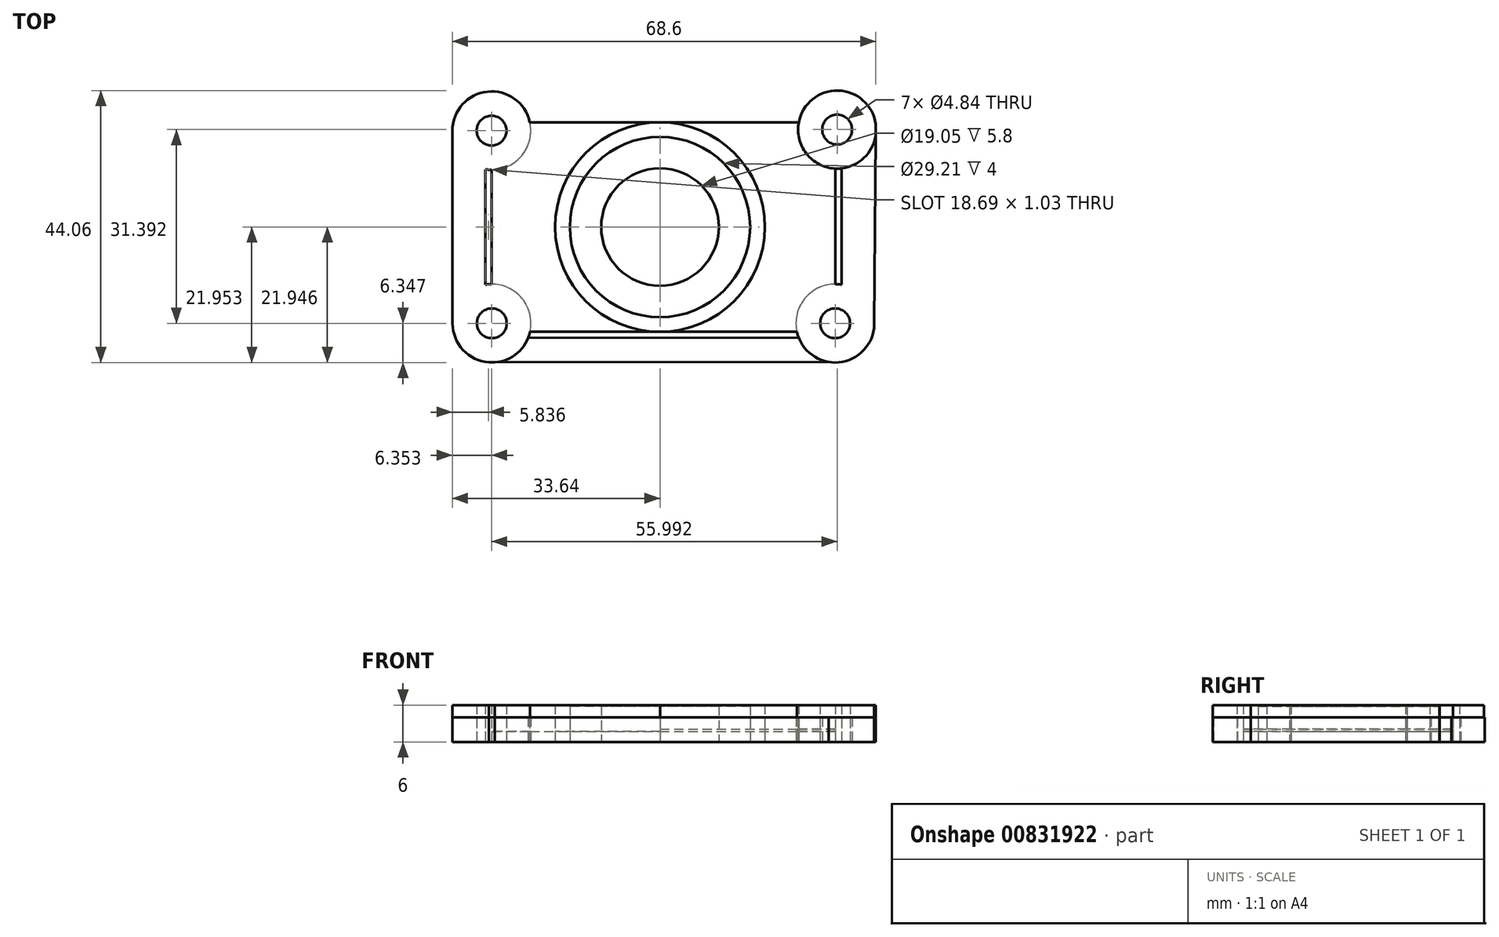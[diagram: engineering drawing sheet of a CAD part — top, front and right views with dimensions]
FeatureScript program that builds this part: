
annotation { "Feature Type Name" : "Feature", "Feature Type Description" : "" }
export const myFeature = defineFeature(function(context is Context, id is Id, definition is map)
    precondition{}
    {
        {
            var Q0;
            Q0=qCreatedBy(makeId("Top.planeOp"),FACE);
            var sketch = newSketch(context, id + "F0", { "sketchPlane" : qUnion([Q0])});
            skCircle(sketch, "E0", {"center": v(14.81, -5.47) * mm, "radius": 6.35 * mm});
            skLineSegment(sketch, "E1", {"start": v(14.81, 0.88) * mm, "end": v(69.45, 0.88) * mm});
            skCircle(sketch, "E2", {"center": v(70.8, -5.3) * mm, "radius": 6.32 * mm});
            skCircle(sketch, "E3", {"center": v(14.85, -36.7) * mm, "radius": 6.35 * mm});
            skLineSegment(sketch, "E4", {"start": v(8.46, -5.47) * mm, "end": v(8.5, -36.7) * mm});
            skCircle(sketch, "E5", {"center": v(70.48, -36.7) * mm, "radius": 6.35 * mm});
            skLineSegment(sketch, "E6", {"start": v(76.83, -36.9) * mm, "end": v(77.06, -4.38) * mm});
            skLineSegment(sketch, "E7.trimOffspring", {"start": v(14.4, -43.03) * mm, "end": v(69.46, -42.96) * mm});
            skCircle(sketch, "E8", {"center": v(42.1, -21.1) * mm, "radius": 16.98 * mm});
            skCircle(sketch, "E9", {"center": v(42.1, -21.1) * mm, "radius": 14.6 * mm});
            skCircle(sketch, "E10", {"center": v(42.1, -21.1) * mm, "radius": 9.53 * mm});
            skLineSegment(sketch, "E11", {"start": v(70.48, -11.62) * mm, "end": v(70.48, -30.34) * mm});
            skLineSegment(sketch, "E12", {"start": v(21.01, -4.1) * mm, "end": v(64.6, -4.1) * mm});
            skLineSegment(sketch, "E13", {"start": v(14.81, -30.34) * mm, "end": v(14.81, -11.82) * mm});
            skLineSegment(sketch, "E14", {"start": v(21.05, -38.08) * mm, "end": v(64.28, -38.08) * mm});
            skLineSegment(sketch, "E15", {"start": v(20.73, -39.09) * mm, "end": v(64.58, -39.03) * mm});
            skLineSegment(sketch, "E16", {"start": v(71.51, -30.43) * mm, "end": v(71.51, -11.58) * mm});
            skLineSegment(sketch, "E17", {"start": v(13.78, -30.43) * mm, "end": v(13.78, -11.74) * mm});
            skLineSegment(sketch, "E18", {"start": v(20.68, -3.04) * mm, "end": v(64.9, -3.04) * mm});
            skCircle(sketch, "E19", {"center": v(14.81, -5.47) * mm, "radius": 2.42 * mm});
            skCircle(sketch, "E20", {"center": v(14.85, -36.7) * mm, "radius": 2.42 * mm});
            skCircle(sketch, "E21", {"center": v(70.48, -36.7) * mm, "radius": 2.42 * mm});
            skCircle(sketch, "E22", {"center": v(70.8, -5.3) * mm, "radius": 2.42 * mm});
            skPoint(sketch, "E23.visualSharp", {"position": v(71.51, -10.41) * mm});
            skPoint(sketch, "E24.orphan", {"position": v(13.78, -10.53) * mm});
            skPoint(sketch, "E25.orphan", {"position": v(14.81, -10.63) * mm});
            skPoint(sketch, "E26.orphan", {"position": v(13.78, -31.65) * mm});
            skPoint(sketch, "E27.orphan", {"position": v(14.81, -31.53) * mm});
            skPoint(sketch, "E28.orphan", {"position": v(70.48, -31.53) * mm});
            skPoint(sketch, "E29.end.orphan", {"position": v(70.48, -10.45) * mm});
            skSolve(sketch);
        }
        {
            var Q0;
            {var subQ0=sQuery(id+"F0.wireOp",EDGE,"E16");var subQ1=sQuery(id+"F0.wireOp",EDGE,"E2");var subQ2=makeQuery(id+"F0.imprint","INTERSECT",VERTEX,{"derivedFrom":[subQ1,subQ0]});Q0=makeQuery(id+"F0.imprint","IMPRINT",FACE,{"disambiguationData":[TD([[makeQuery(id+"F0.imprint","IMPRINT",EDGE,{"disambiguationData":[TD([[subQ2,-1.0]])],"derivedFrom":subQ1}),-1.0]])]});}
            var Q1;
            Q1=makeQuery(id+"F0.imprint","IMPRINT",FACE,{"disambiguationData":[TD([[makeQuery(id+"F0.imprint","IMPRINT",EDGE,{"derivedFrom":sQuery(id+"F0.wireOp",EDGE,"E21")}),-1.0]])]});
            var Q2;
            {var subQ0=sQuery(id+"F0.wireOp",EDGE,"E7.trimOffspring");var subQ1=sQuery(id+"F0.wireOp",EDGE,"E3");var subQ2=makeQuery(id+"F0.imprint","INTERSECT",VERTEX,{"disambiguationData":[OD(1.0)],"derivedFrom":[subQ1,subQ0]});Q2=makeQuery(id+"F0.imprint","IMPRINT",FACE,{"disambiguationData":[TD([[makeQuery(id+"F0.imprint","IMPRINT",EDGE,{"disambiguationData":[TD([[subQ2,-1.0]])],"derivedFrom":subQ1}),-1.0]])]});}
            var Q3;
            Q3=makeQuery(id+"F0.imprint","IMPRINT",FACE,{"disambiguationData":[TD([[makeQuery(id+"F0.imprint","IMPRINT",EDGE,{"derivedFrom":sQuery(id+"F0.wireOp",EDGE,"E20")}),-1.0]])]});
            var Q4;
            {var subQ0=sQuery(id+"F0.wireOp",EDGE,"E4");Q4=makeQuery(id+"F0.imprint","IMPRINT",FACE,{"disambiguationData":[TD([[makeQuery(id+"F0.imprint","IMPRINT",EDGE,{"derivedFrom":subQ0}),1.0]])]});}
            var Q5;
            Q5=makeQuery(id+"F0.imprint","IMPRINT",FACE,{"disambiguationData":[TD([[makeQuery(id+"F0.imprint","IMPRINT",EDGE,{"derivedFrom":sQuery(id+"F0.wireOp",EDGE,"E19")}),-1.0]])]});
            var Q6;
            {var subQ0=sQuery(id+"F0.wireOp",EDGE,"E1");Q6=makeQuery(id+"F0.imprint","IMPRINT",FACE,{"disambiguationData":[TD([[makeQuery(id+"F0.imprint","IMPRINT",EDGE,{"derivedFrom":subQ0}),-1.0]])]});}
            var Q7;
            {var subQ10=sQuery(id+"F0.wireOp",EDGE,"ZcBLGhaq-u4ml-COmK-nmpy-0ZbfGJL8DPDr");Q7=makeQuery(id+"F0.imprint","IMPRINT",FACE,{"disambiguationData":[TD([[makeQuery(id+"F0.imprint","IMPRINT",EDGE,{"derivedFrom":subQ10}),1.0]])]});}
            var Q8;
            {var subQ0=sQuery(id+"F0.wireOp",EDGE,"E12");var subQ1=sQuery(id+"F0.wireOp",EDGE,"E0");var subQ2=makeQuery(id+"F0.imprint","INTERSECT",VERTEX,{"derivedFrom":[subQ1,subQ0]});Q8=makeQuery(id+"F0.imprint","IMPRINT",FACE,{"disambiguationData":[TD([[makeQuery(id+"F0.imprint","IMPRINT",EDGE,{"disambiguationData":[TD([[subQ2,1.0]])],"derivedFrom":subQ1}),-1.0]])]});}
            var Q9;
            {var subQ1=sQuery(id+"F0.wireOp",EDGE,"E2");var subQ9=sQuery(id+"F0.wireOp",EDGE,"E12");var subQ11=makeQuery(id+"F0.imprint","INTERSECT",VERTEX,{"derivedFrom":[subQ1,subQ9]});Q9=makeQuery(id+"F0.imprint","IMPRINT",FACE,{"disambiguationData":[TD([[makeQuery(id+"F0.imprint","IMPRINT",EDGE,{"disambiguationData":[TD([[subQ11,-1.0]])],"derivedFrom":subQ1}),-1.0]])]});}
            extrude(context, id + "F1", {"entities" : qUnion([Q0, Q1, Q2, Q3, Q4, Q5, Q6, Q7, Q8, Q9]), "depth" : 6 * mm, "offsetDistance" : 25 * mm});
        }
        {
            var Q0;
            Q0=makeQuery(id+"F0.imprint","IMPRINT",FACE,{"disambiguationData":[TD([[makeQuery(id+"F0.imprint","IMPRINT",EDGE,{"derivedFrom":sQuery(id+"F0.wireOp",EDGE,"E9")}),1.0]])]});
            extrude(context, id + "F2", {"entities" : qUnion([Q0]), "depth" : 5.8 * mm, "offsetDistance" : 25 * mm});
        }
        {
            var Q0;
            Q0=makeQuery(id+"F0.imprint","IMPRINT",FACE,{"disambiguationData":[TD([[makeQuery(id+"F0.imprint","IMPRINT",EDGE,{"derivedFrom":sQuery(id+"F0.wireOp",EDGE,"E9")}),-1.0]])]});
            extrude(context, id + "F3", {"entities" : qUnion([Q0]), "depth" : 4 * mm, "offsetDistance" : 25 * mm});
        }
        {
            var Q0;
            Q0=makeQuery(id+"F0.imprint","IMPRINT",FACE,{"disambiguationData":[TD([[makeQuery(id+"F0.imprint","IMPRINT",EDGE,{"derivedFrom":sQuery(id+"F0.wireOp",EDGE,"E21")}),-1.0]])]});
            var Q1;
            {var subQ0=sQuery(id+"F0.wireOp",EDGE,"E16");Q1=makeQuery(id+"F0.imprint","IMPRINT",FACE,{"disambiguationData":[TD([[makeQuery(id+"F0.imprint","IMPRINT",EDGE,{"derivedFrom":subQ0}),-1.0]])]});}
            var Q2;
            Q2=makeQuery(id+"F0.imprint","IMPRINT",FACE,{"disambiguationData":[TD([[makeQuery(id+"F0.imprint","IMPRINT",EDGE,{"derivedFrom":sQuery(id+"F0.wireOp",EDGE,"E22")}),-1.0]])]});
            var Q3;
            {var subQ0=sQuery(id+"F0.wireOp",EDGE,"E1");Q3=makeQuery(id+"F0.imprint","IMPRINT",FACE,{"disambiguationData":[TD([[makeQuery(id+"F0.imprint","IMPRINT",EDGE,{"derivedFrom":subQ0}),-1.0]])]});}
            var Q4;
            Q4=makeQuery(id+"F0.imprint","IMPRINT",FACE,{"disambiguationData":[TD([[makeQuery(id+"F0.imprint","IMPRINT",EDGE,{"derivedFrom":sQuery(id+"F0.wireOp",EDGE,"E19")}),-1.0]])]});
            var Q5;
            {var subQ0=sQuery(id+"F0.wireOp",EDGE,"E4");Q5=makeQuery(id+"F0.imprint","IMPRINT",FACE,{"disambiguationData":[TD([[makeQuery(id+"F0.imprint","IMPRINT",EDGE,{"derivedFrom":subQ0}),1.0]])]});}
            var Q6;
            Q6=makeQuery(id+"F0.imprint","IMPRINT",FACE,{"disambiguationData":[TD([[makeQuery(id+"F0.imprint","IMPRINT",EDGE,{"derivedFrom":sQuery(id+"F0.wireOp",EDGE,"E20")}),-1.0]])]});
            var Q7;
            {var subQ0=sQuery(id+"F0.wireOp",EDGE,"E15");Q7=makeQuery(id+"F0.imprint","IMPRINT",FACE,{"disambiguationData":[TD([[makeQuery(id+"F0.imprint","IMPRINT",EDGE,{"derivedFrom":subQ0}),-1.0]])]});}
            extrude(context, id + "F4", {"entities" : qUnion([Q0, Q1, Q2, Q3, Q4, Q5, Q6, Q7]), "depth" : 4 * mm, "offsetDistance" : 25 * mm});
        }
        {
            var Q0;
            {var subQ7=sQuery(id+"F0.wireOp",EDGE,"E13");Q0=makeQuery(id+"F0.imprint","IMPRINT",FACE,{"disambiguationData":[TD([[makeQuery(id+"F0.imprint","IMPRINT",EDGE,{"derivedFrom":subQ7}),-1.0]])]});}
            var Q1;
            {var subQ5=sQuery(id+"F0.wireOp",EDGE,"E11");Q1=makeQuery(id+"F0.imprint","IMPRINT",FACE,{"disambiguationData":[TD([[makeQuery(id+"F0.imprint","IMPRINT",EDGE,{"derivedFrom":subQ5}),-1.0]])]});}
            extrude(context, id + "F5", {"entities" : qUnion([Q0, Q1]), "depth" : 1.7 * mm, "offsetDistance" : 25 * mm});
        }
        {
            var Q0;
            Q0=makeQuery(id+"F5.opExtrude","CAP_FACE",FACE,{"disambiguationData":[OSD([sQuery(id+"F0.wireOp",EDGE,"E2"),sQuery(id+"F0.wireOp",EDGE,"E5"),sQuery(id+"F0.wireOp",EDGE,"E8"),sQuery(id+"F0.wireOp",EDGE,"E11"),sQuery(id+"F0.wireOp",EDGE,"E12"),sQuery(id+"F0.wireOp",EDGE,"E14")])],"isStart":false});
            extrude(context, id + "F6", {"entities" : qUnion([Q0]), "depth" : 0.4 * mm, "offsetDistance" : 25 * mm});
        }
    });
